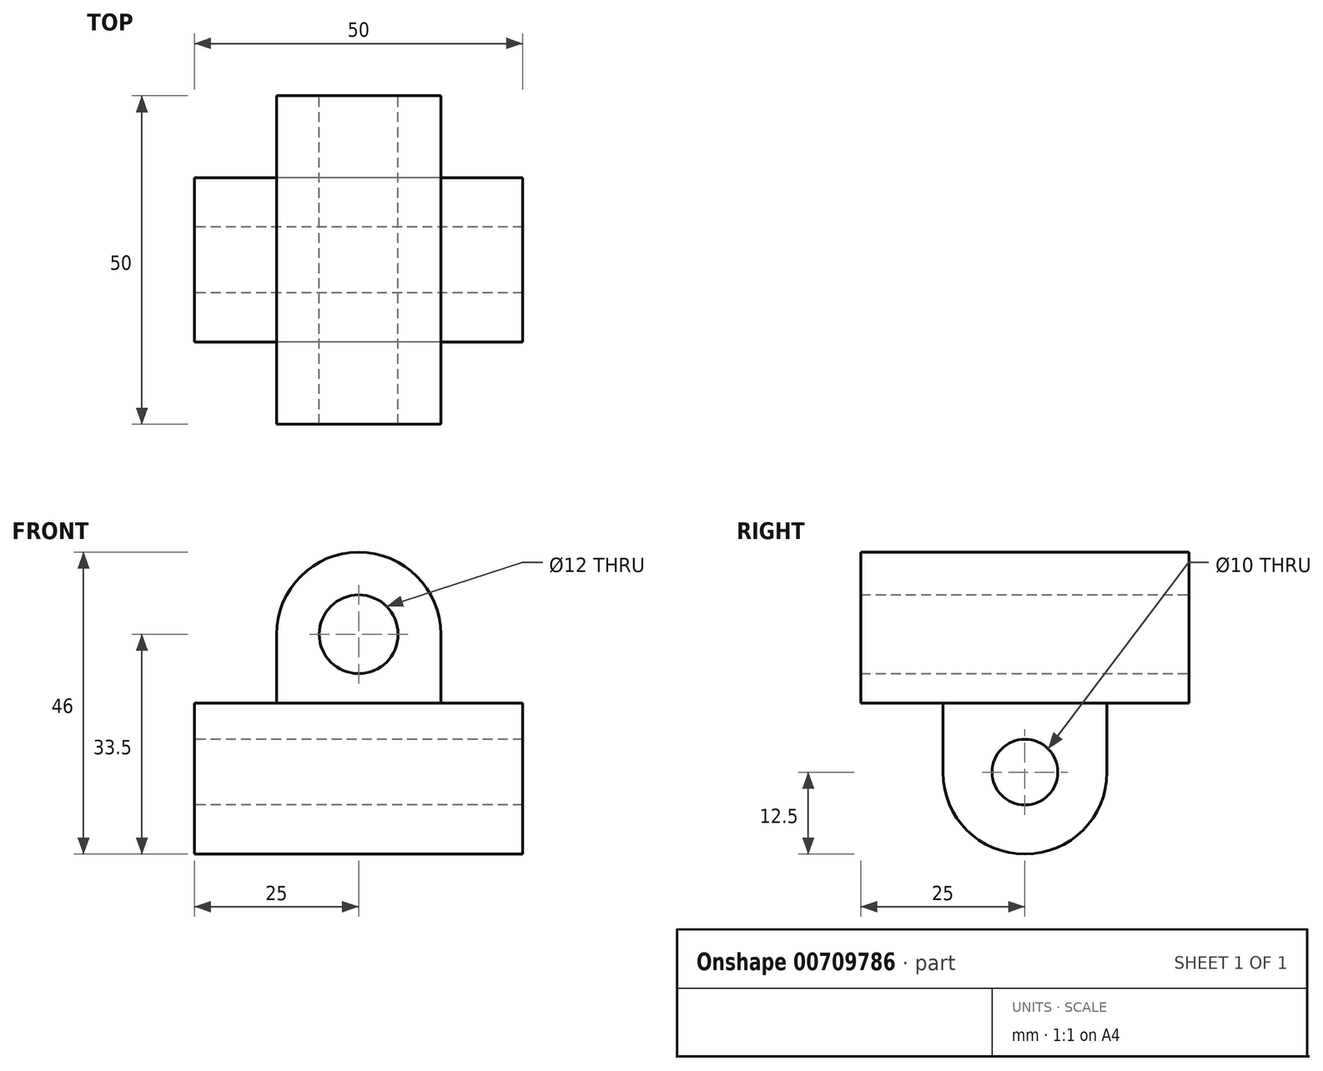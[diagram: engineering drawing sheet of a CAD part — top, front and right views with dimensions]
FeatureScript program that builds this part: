
annotation { "Feature Type Name" : "Feature", "Feature Type Description" : "" }
export const myFeature = defineFeature(function(context is Context, id is Id, definition is map)
    precondition{}
    {
        {
            var Q0;
            Q0=qCreatedBy(makeId("Front.planeOp"),FACE);
            var sketch = newSketch(context, id + "F0", { "sketchPlane" : qUnion([Q0])});
            skCircle(sketch, "E0", {"center": v(0, 20) * mm, "radius": 6 * mm});
            skCircle(sketch, "E1", {"center": v(0, 20) * mm, "radius": 12.5 * mm});
            skLineSegment(sketch, "E2", {"start": v(-12.5, 20) * mm, "end": v(-12.5, 9.5) * mm});
            skLineSegment(sketch, "E3", {"start": v(-12.5, 9.5) * mm, "end": v(12.5, 9.5) * mm});
            skLineSegment(sketch, "E4", {"start": v(12.5, 9.5) * mm, "end": v(12.5, 20) * mm});
            skCircle(sketch, "E5", {"center": v(0, 20) * mm, "radius": 9.5 * mm, "construction": true});
            skSolve(sketch);
        }
        {
            var Q0;
            Q0=makeQuery(id+"F0.imprint","IMPRINT",FACE,{"disambiguationData":[TD([[makeQuery(id+"F0.imprint","IMPRINT",EDGE,{"derivedFrom":sQuery(id+"F0.wireOp",EDGE,"E0")}),-1.0]])]});
            var Q1;
            {var subQ0=sQuery(id+"F0.wireOp",EDGE,"E4");Q1=makeQuery(id+"F0.imprint","IMPRINT",FACE,{"disambiguationData":[TD([[makeQuery(id+"F0.imprint","IMPRINT",EDGE,{"derivedFrom":subQ0}),1.0]])]});}
            var Q2;
            {var subQ0=sQuery(id+"F0.wireOp",EDGE,"E2");Q2=makeQuery(id+"F0.imprint","IMPRINT",FACE,{"disambiguationData":[TD([[makeQuery(id+"F0.imprint","IMPRINT",EDGE,{"derivedFrom":subQ0}),1.0]])]});}
            extrude(context, id + "F1", {"entities" : qUnion([Q0, Q1, Q2]), "endBound" : BoundingType.SYMMETRIC, "depth" : 50 * mm, "offsetDistance" : 25 * mm});
        }
        {
            var Q0;
            Q0=qCreatedBy(makeId("Right.planeOp"),FACE);
            var sketch = newSketch(context, id + "F2", { "sketchPlane" : qUnion([Q0])});
            skCircle(sketch, "E6", {"center": v(0, -1) * mm, "radius": 5 * mm});
            skCircle(sketch, "E7", {"center": v(0, -1) * mm, "radius": 12.5 * mm});
            skLineSegment(sketch, "E8", {"start": v(-25, 32.5) * mm, "end": v(25, 32.5) * mm});
            skLineSegment(sketch, "E9", {"start": v(-12.5, -1) * mm, "end": v(-12.5, 9.5) * mm});
            skLineSegment(sketch, "E10", {"start": v(12.5, -1) * mm, "end": v(12.5, 9.5) * mm});
            skCircle(sketch, "E11", {"center": v(0, -1) * mm, "radius": 9.5 * mm, "construction": true});
            skLineSegment(sketch, "E12.0.1", {"start": v(25, 9.5) * mm, "end": v(-25, 9.5) * mm});
            skLineSegment(sketch, "E12.0.3", {"start": v(-25, 9.5) * mm, "end": v(25, 9.5) * mm});
            skSolve(sketch);
        }
        {
            var Q0;
            {var subQ0=sQuery(id+"F2.wireOp",EDGE,"E6");Q0=makeQuery(id+"F2.imprint","IMPRINT",FACE,{"disambiguationData":[TD([[makeQuery(id+"F2.imprint","IMPRINT",EDGE,{"derivedFrom":subQ0}),-1.0]])]});}
            var Q1;
            {var subQ0=sQuery(id+"F2.wireOp",EDGE,"8a71cc45-00db-4389-b25f-f17406de7790");var subQ1=sQuery(id+"F2.wireOp",EDGE,"E7");var subQ2=makeQuery(id+"F2.imprint","INTERSECT",VERTEX,{"disambiguationData":[OD(0.0)],"derivedFrom":[subQ1,subQ0]});Q1=makeQuery(id+"F2.imprint","IMPRINT",FACE,{"disambiguationData":[TD([[makeQuery(id+"F2.imprint","IMPRINT",EDGE,{"disambiguationData":[TD([[subQ2,-1.0]])],"derivedFrom":subQ1}),1.0]])]});}
            var Q2;
            {var subQ0=sQuery(id+"F2.wireOp",EDGE,"E9");Q2=makeQuery(id+"F2.imprint","IMPRINT",FACE,{"disambiguationData":[TD([[makeQuery(id+"F2.imprint","IMPRINT",EDGE,{"derivedFrom":subQ0}),-1.0]])]});}
            var Q3;
            {var subQ0=sQuery(id+"F2.wireOp",EDGE,"E10");Q3=makeQuery(id+"F2.imprint","IMPRINT",FACE,{"disambiguationData":[TD([[makeQuery(id+"F2.imprint","IMPRINT",EDGE,{"derivedFrom":subQ0}),1.0]])]});}
            extrude(context, id + "F3", {"entities" : qUnion([Q0, Q1, Q2, Q3]), "operationType" : NewBodyOperationType.ADD, "endBound" : BoundingType.SYMMETRIC, "depth" : 50 * mm, "offsetDistance" : 25 * mm});
        }
    });
